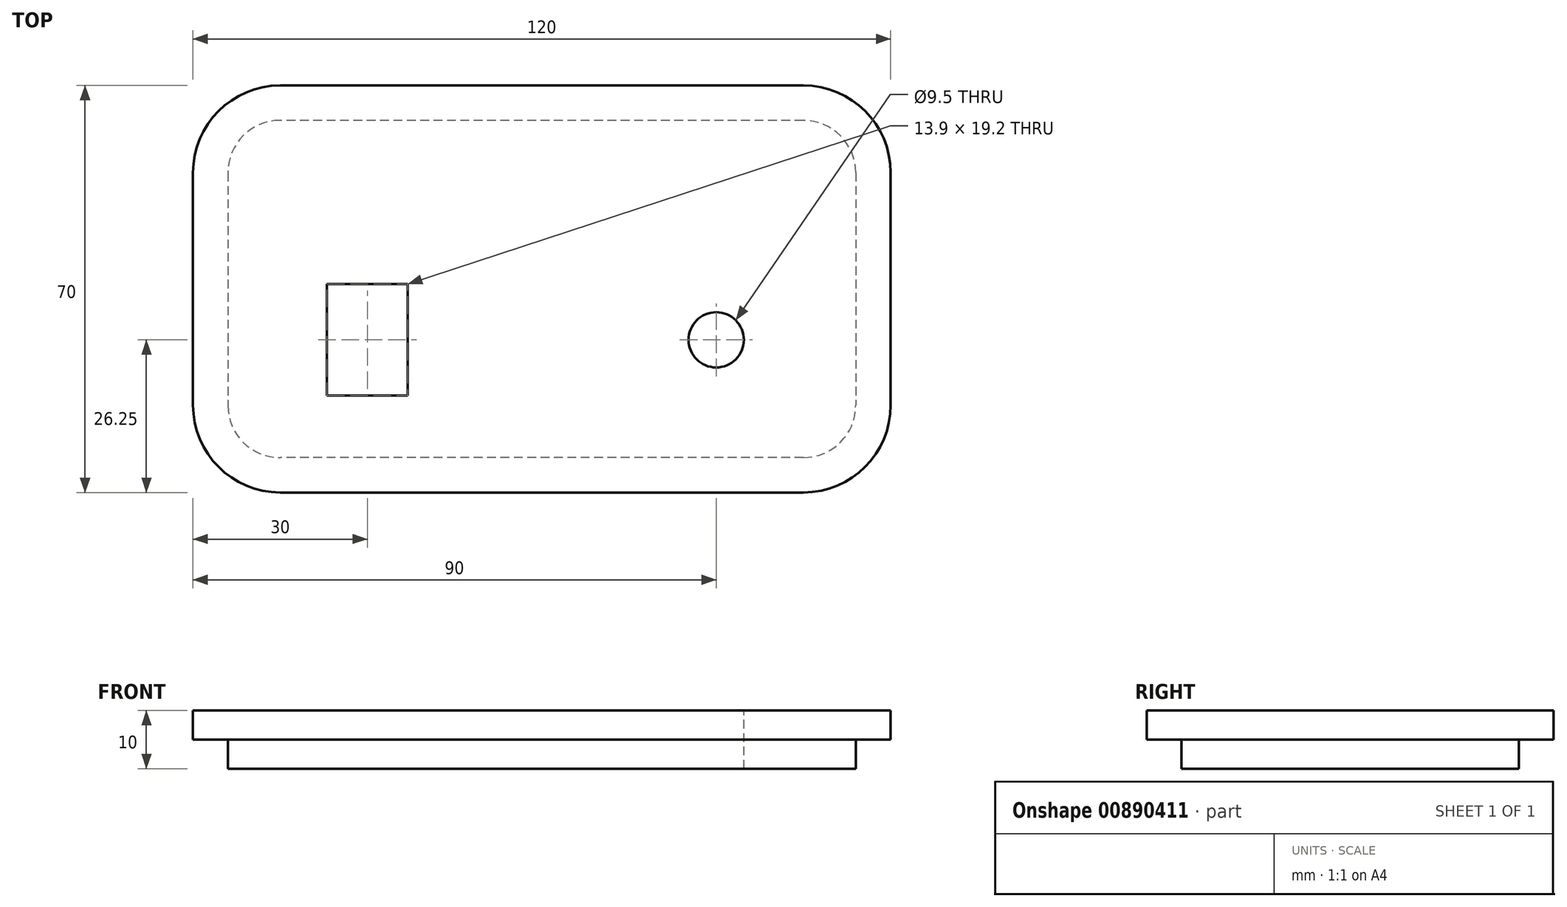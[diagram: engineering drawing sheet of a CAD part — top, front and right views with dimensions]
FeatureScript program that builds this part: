
annotation { "Feature Type Name" : "Feature", "Feature Type Description" : "" }
export const myFeature = defineFeature(function(context is Context, id is Id, definition is map)
    precondition{}
    {
        {
            var Q0;
            Q0=qCreatedBy(makeId("Top.planeOp"),FACE);
            cPlane(context, id + "F0", {"entities" : qUnion([Q0]), "cplaneType" : CPlaneType.OFFSET, "offset" : 2.5 * mm, "width" : 150 * mm, "height" : 150 * mm});
        }
        {
            var Q0;
            Q0=qCreatedBy(id+"F0.planeOp",FACE);
            var sketch = newSketch(context, id + "F1", { "sketchPlane" : qUnion([Q0])});
            skLineSegment(sketch, "E0.bottom", {"start": v(45, 30) * mm, "end": v(-45, 30) * mm});
            skLineSegment(sketch, "E0.top", {"start": v(45, -30) * mm, "end": v(-45, -30) * mm});
            skLineSegment(sketch, "E0.left", {"start": v(55, 20) * mm, "end": v(55, -20) * mm});
            skLineSegment(sketch, "E0.right", {"start": v(-55, 20) * mm, "end": v(-55, -20) * mm});
            skPoint(sketch, "E0.middle", {"position": v(0, 0) * mm});
            skPoint(sketch, "E1.visualSharp", {"position": v(-55, 30) * mm});
            skArc(sketch, "E1.filletArc", {"start": v(-45, 30) * mm, "mid": v(-52.07, 27.07) * mm, "end": v(-55, 20) * mm});
            skPoint(sketch, "E2.visualSharp", {"position": v(-55, -30) * mm});
            skArc(sketch, "E2.filletArc", {"start": v(-55, -20) * mm, "mid": v(-52.07, -27.07) * mm, "end": v(-45, -30) * mm});
            skPoint(sketch, "E3.visualSharp", {"position": v(55, -30) * mm});
            skArc(sketch, "E3.filletArc", {"start": v(45, -30) * mm, "mid": v(52.07, -27.07) * mm, "end": v(55, -20) * mm});
            skPoint(sketch, "E4.visualSharp", {"position": v(55, 30) * mm});
            skArc(sketch, "E4.filletArc", {"start": v(55, 20) * mm, "mid": v(52.07, 27.07) * mm, "end": v(45, 30) * mm});
            skLineSegment(sketch, "E5.bottom", {"start": v(-45, 35) * mm, "end": v(45, 35) * mm});
            skLineSegment(sketch, "E5.top", {"start": v(-45, -35) * mm, "end": v(45, -35) * mm});
            skLineSegment(sketch, "E5.left", {"start": v(-60, 20) * mm, "end": v(-60, -20) * mm});
            skLineSegment(sketch, "E5.right", {"start": v(60, 20) * mm, "end": v(60, -20) * mm});
            skPoint(sketch, "E6.visualSharp", {"position": v(-60, 35) * mm});
            skArc(sketch, "E6.filletArc", {"start": v(-45, 35) * mm, "mid": v(-55.6, 30.6) * mm, "end": v(-60, 20) * mm});
            skPoint(sketch, "E7.visualSharp", {"position": v(-60, -35) * mm});
            skArc(sketch, "E7.filletArc", {"start": v(-60, -20) * mm, "mid": v(-55.6, -30.6) * mm, "end": v(-45, -35) * mm});
            skPoint(sketch, "E8.visualSharp", {"position": v(60, -35) * mm});
            skArc(sketch, "E8.filletArc", {"start": v(45, -35) * mm, "mid": v(55.6, -30.6) * mm, "end": v(60, -20) * mm});
            skPoint(sketch, "E9.visualSharp", {"position": v(60, 35) * mm});
            skArc(sketch, "E9.filletArc", {"start": v(60, 20) * mm, "mid": v(55.6, 30.6) * mm, "end": v(45, 35) * mm});
            skLineSegment(sketch, "E10.bottom", {"start": v(45, 29) * mm, "end": v(-45, 29) * mm});
            skLineSegment(sketch, "E10.top", {"start": v(45, -29) * mm, "end": v(-45, -29) * mm});
            skLineSegment(sketch, "E10.left", {"start": v(54, 20) * mm, "end": v(54, -20) * mm});
            skLineSegment(sketch, "E10.right", {"start": v(-54, 20) * mm, "end": v(-54, -20) * mm});
            skArc(sketch, "E11.filletArc", {"start": v(-45, 29) * mm, "mid": v(-51.36, 26.36) * mm, "end": v(-54, 20) * mm});
            skArc(sketch, "E12.filletArc", {"start": v(-54, -20) * mm, "mid": v(-51.36, -26.36) * mm, "end": v(-45, -29) * mm});
            skArc(sketch, "E13.filletArc", {"start": v(45, -29) * mm, "mid": v(51.36, -26.36) * mm, "end": v(54, -20) * mm});
            skArc(sketch, "E14.filletArc", {"start": v(54, 20) * mm, "mid": v(51.36, 26.36) * mm, "end": v(45, 29) * mm});
            skSolve(sketch);
        }
        {
            var Q0;
            Q0=makeQuery(id+"F1.imprint","IMPRINT",FACE,{"disambiguationData":[TD([[makeQuery(id+"F1.imprint","IMPRINT",EDGE,{"derivedFrom":sQuery(id+"F1.wireOp",EDGE,"E0.bottom")}),-1.0]])]});
            var Q1;
            Q1=makeQuery(id+"F1.imprint","IMPRINT",FACE,{"disambiguationData":[TD([[makeQuery(id+"F1.imprint","IMPRINT",EDGE,{"derivedFrom":sQuery(id+"F1.wireOp",EDGE,"E10.bottom")}),1.0]])]});
            var Q2;
            Q2=makeQuery(id+"F1.imprint","IMPRINT",FACE,{"disambiguationData":[TD([[makeQuery(id+"F1.imprint","IMPRINT",EDGE,{"derivedFrom":sQuery(id+"F1.wireOp",EDGE,"E0.bottom")}),1.0]])]});
            extrude(context, id + "F2", {"entities" : qUnion([Q0, Q1, Q2]), "depth" : 5 * mm, "offsetDistance" : 25 * mm});
        }
        {
            var Q0;
            Q0=makeQuery(id+"F1.imprint","IMPRINT",FACE,{"disambiguationData":[TD([[makeQuery(id+"F1.imprint","IMPRINT",EDGE,{"derivedFrom":sQuery(id+"F1.wireOp",EDGE,"E10.bottom")}),1.0]])]});
            extrude(context, id + "F3", {"entities" : qUnion([Q0]), "operationType" : NewBodyOperationType.ADD, "oppositeDirection" : true, "depth" : 5 * mm, "offsetDistance" : 25 * mm});
        }
        {
            var Q0;
            Q0=makeQuery(id+"F2.opExtrude","CAP_FACE",FACE,{"disambiguationData":[OSD([sQuery(id+"F1.wireOp",EDGE,"E5.bottom"),sQuery(id+"F1.wireOp",EDGE,"E5.top"),sQuery(id+"F1.wireOp",EDGE,"E5.left"),sQuery(id+"F1.wireOp",EDGE,"E5.right"),sQuery(id+"F1.wireOp",EDGE,"E6.filletArc"),sQuery(id+"F1.wireOp",EDGE,"E7.filletArc"),sQuery(id+"F1.wireOp",EDGE,"E8.filletArc"),sQuery(id+"F1.wireOp",EDGE,"E9.filletArc")])],"isStart":false});
            var sketch = newSketch(context, id + "F4", { "sketchPlane" : qUnion([Q0])});
            skLineSegment(sketch, "E15.bottom", {"start": v(-23.05, 0.85) * mm, "end": v(-36.95, 0.85) * mm});
            skLineSegment(sketch, "E15.top", {"start": v(-23.05, -18.35) * mm, "end": v(-36.95, -18.35) * mm});
            skLineSegment(sketch, "E15.left", {"start": v(-23.05, 0.85) * mm, "end": v(-23.05, -18.35) * mm});
            skLineSegment(sketch, "E15.right", {"start": v(-36.95, 0.85) * mm, "end": v(-36.95, -18.35) * mm});
            skCircle(sketch, "E16", {"center": v(30, -8.75) * mm, "radius": 4.75 * mm});
            skPoint(sketch, "E17", {"position": v(-36.95, -8.75) * mm});
            skPoint(sketch, "E18", {"position": v(-23.05, -8.75) * mm});
            skPoint(sketch, "E19", {"position": v(25.25, -8.75) * mm});
            skPoint(sketch, "E20", {"position": v(34.75, -8.75) * mm});
            skLineSegment(sketch, "E21", {"start": v(-60, 0) * mm, "end": v(60, 0) * mm, "construction": true});
            skLineSegment(sketch, "E22", {"start": v(0, 35) * mm, "end": v(0, -35) * mm, "construction": true});
            skLineSegment(sketch, "E23", {"start": v(-60, 35) * mm, "end": v(60, 35) * mm, "construction": true});
            skLineSegment(sketch, "E24", {"start": v(60, 35) * mm, "end": v(60, -35) * mm, "construction": true});
            skLineSegment(sketch, "E25", {"start": v(60, -35) * mm, "end": v(-60, -35) * mm, "construction": true});
            skLineSegment(sketch, "E26", {"start": v(-60, 35) * mm, "end": v(-60, -35) * mm, "construction": true});
            skLineSegment(sketch, "E27", {"start": v(-60, 0) * mm, "end": v(-60, 35) * mm, "construction": true});
            skLineSegment(sketch, "E28", {"start": v(-60, 35) * mm, "end": v(0, 35) * mm, "construction": true});
            skLineSegment(sketch, "E29", {"start": v(0, 35) * mm, "end": v(60, 35) * mm, "construction": true});
            skLineSegment(sketch, "E30", {"start": v(60, 35) * mm, "end": v(60, 0) * mm, "construction": true});
            skLineSegment(sketch, "E31", {"start": v(60, 0) * mm, "end": v(60, -35) * mm, "construction": true});
            skLineSegment(sketch, "E32", {"start": v(60, -35) * mm, "end": v(0, -35) * mm, "construction": true});
            skLineSegment(sketch, "E33", {"start": v(0, -35) * mm, "end": v(-60, -35) * mm, "construction": true});
            skLineSegment(sketch, "E34", {"start": v(-60, 17.5) * mm, "end": v(0, 17.5) * mm, "construction": true});
            skLineSegment(sketch, "E35", {"start": v(0, 17.5) * mm, "end": v(60, 17.5) * mm, "construction": true});
            skLineSegment(sketch, "E36", {"start": v(-30, 35) * mm, "end": v(-30, -35) * mm, "construction": true});
            skLineSegment(sketch, "E37", {"start": v(30, 35) * mm, "end": v(30, -35) * mm, "construction": true});
            skLineSegment(sketch, "E38", {"start": v(-60, -35) * mm, "end": v(-60, 0) * mm, "construction": true});
            skLineSegment(sketch, "E39", {"start": v(60, -17.5) * mm, "end": v(-60, -17.5) * mm, "construction": true});
            skLineSegment(sketch, "E40", {"start": v(-60, 0) * mm, "end": v(-60, -17.5) * mm, "construction": true});
            skLineSegment(sketch, "E41", {"start": v(60, 0) * mm, "end": v(60, -17.5) * mm, "construction": true});
            skLineSegment(sketch, "E42", {"start": v(60, -8.75) * mm, "end": v(-60, -8.75) * mm, "construction": true});
            skPoint(sketch, "E43", {"position": v(-30, 0.85) * mm});
            skPoint(sketch, "E44", {"position": v(-30, -18.35) * mm});
            skSolve(sketch);
        }
        {
            var Q0;
            Q0 = qSketchRegion(id + "F4", true);
            extrude(context, id + "F5", {"entities" : qUnion([Q0]), "operationType" : NewBodyOperationType.REMOVE, "endBound" : BoundingType.UP_TO_NEXT, "oppositeDirection" : true, "depth" : 25 * mm, "offsetDistance" : 25 * mm});
        }
    });
